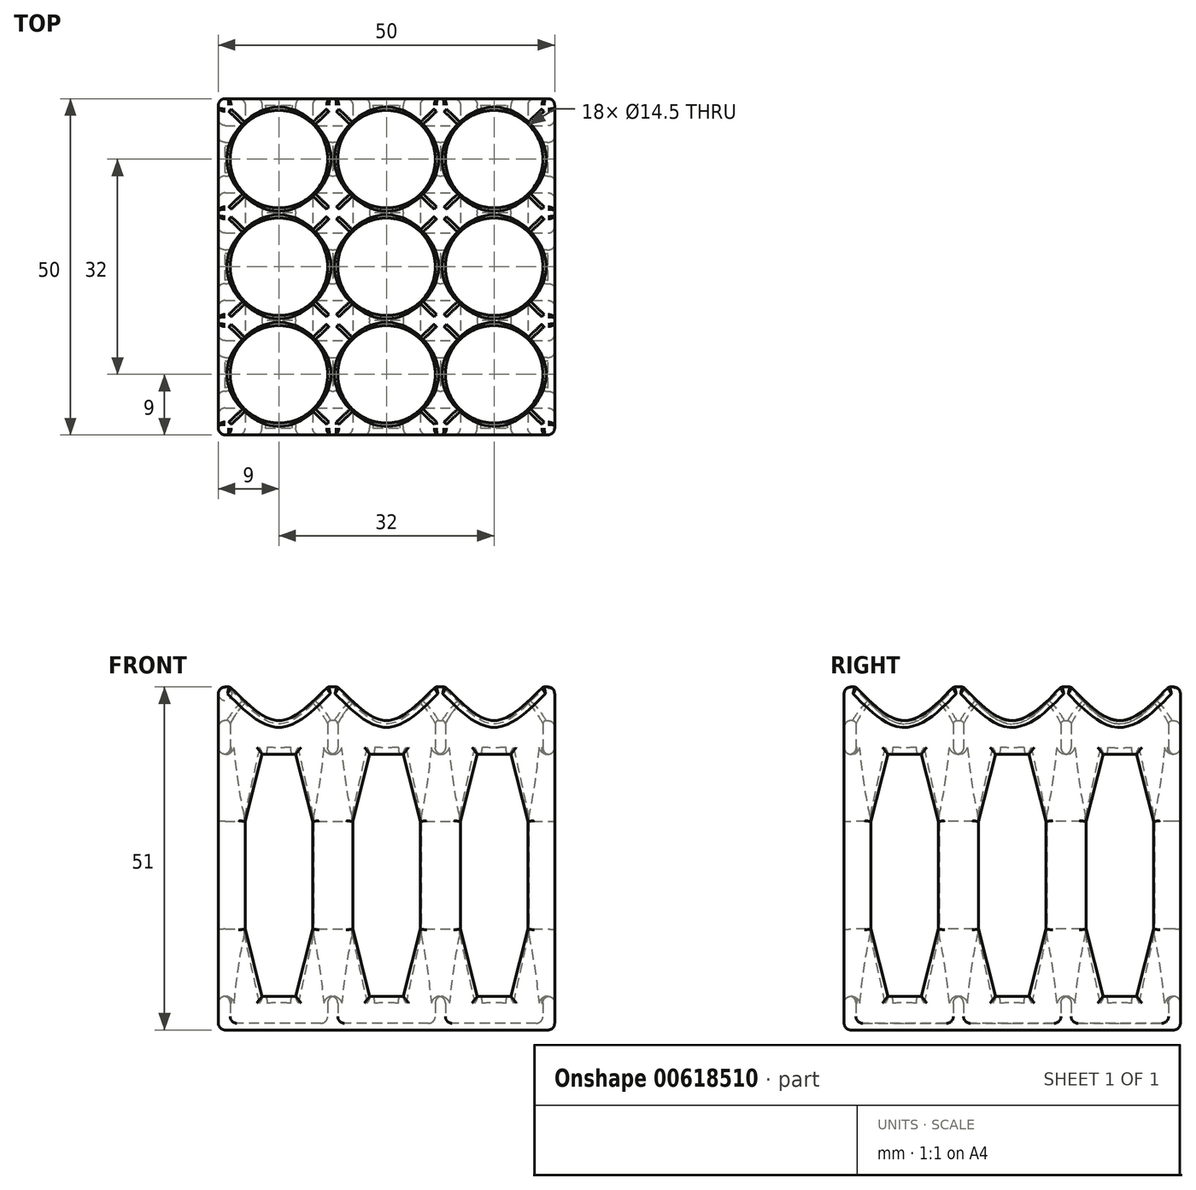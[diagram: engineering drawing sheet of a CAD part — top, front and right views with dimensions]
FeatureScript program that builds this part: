
annotation { "Feature Type Name" : "Feature", "Feature Type Description" : "" }
export const myFeature = defineFeature(function(context is Context, id is Id, definition is map)
    precondition{}
    {
        {
            var Q0;
            Q0=qCreatedBy(makeId("Top.planeOp"),FACE);
            var sketch = newSketch(context, id + "F0", { "sketchPlane" : qUnion([Q0])});
            skLineSegment(sketch, "E0.bottom", {"start": v(24, -24) * mm, "end": v(-24, -24) * mm});
            skLineSegment(sketch, "E0.top", {"start": v(24, 24) * mm, "end": v(-24, 24) * mm});
            skLineSegment(sketch, "E0.left", {"start": v(24, -24) * mm, "end": v(24, 24) * mm});
            skLineSegment(sketch, "E0.right", {"start": v(-24, -24) * mm, "end": v(-24, 24) * mm});
            skPoint(sketch, "E0.middle", {"position": v(0, 0) * mm});
            skLineSegment(sketch, "E1.0", {"start": v(25, 25) * mm, "end": v(-25, 25) * mm});
            skLineSegment(sketch, "E1.1", {"start": v(25, -25) * mm, "end": v(25, 25) * mm});
            skLineSegment(sketch, "E1.2", {"start": v(25, -25) * mm, "end": v(-25, -25) * mm});
            skLineSegment(sketch, "E1.3", {"start": v(-25, -25) * mm, "end": v(-25, 25) * mm});
            skLineSegment(sketch, "E2", {"start": v(-8, 24) * mm, "end": v(-8, -24) * mm});
            skLineSegment(sketch, "E3", {"start": v(8, 24) * mm, "end": v(8, -24) * mm});
            skLineSegment(sketch, "E4", {"start": v(-24, -8) * mm, "end": v(24, -8) * mm});
            skLineSegment(sketch, "E5", {"start": v(-24, 8) * mm, "end": v(24, 8) * mm});
            skPoint(sketch, "E6", {"position": v(-16, -16) * mm});
            skPoint(sketch, "E7", {"position": v(0, -16) * mm});
            skPoint(sketch, "E8", {"position": v(16, -16) * mm});
            skPoint(sketch, "E9", {"position": v(16, 0) * mm});
            skPoint(sketch, "E10", {"position": v(-16, 0) * mm});
            skPoint(sketch, "E11", {"position": v(-16, 16) * mm});
            skPoint(sketch, "E12", {"position": v(0, 16) * mm});
            skPoint(sketch, "E13", {"position": v(16, 16) * mm});
            skPoint(sketch, "E14", {"position": v(-8, 8) * mm});
            skPoint(sketch, "E15", {"position": v(8, 8) * mm});
            skPoint(sketch, "E16", {"position": v(-8, -8) * mm});
            skPoint(sketch, "E17", {"position": v(8, -8) * mm});
            skCircle(sketch, "E18", {"center": v(-16, -16) * mm, "radius": 7.25 * mm});
            skCircle(sketch, "E19", {"center": v(0, -16) * mm, "radius": 7.25 * mm});
            skCircle(sketch, "E20", {"center": v(16, -16) * mm, "radius": 7.25 * mm});
            skCircle(sketch, "E21", {"center": v(16, 0) * mm, "radius": 7.25 * mm});
            skCircle(sketch, "E22", {"center": v(0, 0) * mm, "radius": 7.25 * mm});
            skCircle(sketch, "E23", {"center": v(-16, 0) * mm, "radius": 7.25 * mm});
            skCircle(sketch, "E24", {"center": v(-16, 16) * mm, "radius": 7.25 * mm});
            skCircle(sketch, "E25", {"center": v(0, 16) * mm, "radius": 7.25 * mm});
            skCircle(sketch, "E26", {"center": v(16, 16) * mm, "radius": 7.25 * mm});
            skSolve(sketch);
        }
        {
            var Q0;
            Q0=qCreatedBy(makeId("Front.planeOp"),FACE);
            var sketch = newSketch(context, id + "F1", { "sketchPlane" : qUnion([Q0])});
            skPoint(sketch, "E27", {"position": v(-25, 0) * mm});
            skPoint(sketch, "E28", {"position": v(25, 0) * mm});
            skLineSegment(sketch, "E29.bottom", {"start": v(-25, 0) * mm, "end": v(25, 0) * mm});
            skLineSegment(sketch, "E29.top", {"start": v(-25, 50) * mm, "end": v(25, 50) * mm});
            skLineSegment(sketch, "E29.left", {"start": v(-25, 0) * mm, "end": v(-25, 50) * mm});
            skLineSegment(sketch, "E29.right", {"start": v(25, 0) * mm, "end": v(25, 50) * mm});
            skLineSegment(sketch, "E30.top", {"start": v(-25, -1) * mm, "end": v(25, -1) * mm});
            skLineSegment(sketch, "E30.left", {"start": v(-25, 0) * mm, "end": v(-25, -1) * mm});
            skLineSegment(sketch, "E30.right", {"start": v(25, 0) * mm, "end": v(25, -1) * mm});
            skSolve(sketch);
        }
        {
            var Q0;
            Q0=qSketchRegion(id+"F1",true);
            var Q1;
            Q1=sQuery(id+"F0.wireOp",VERTEX,"E1.3.start");
            var Q2;
            Q2=sQuery(id+"F0.wireOp",VERTEX,"E1.0.end");
            extrude(context, id + "F2", {"entities" : qUnion([Q0]), "endBound" : BoundingType.UP_TO_VERTEX, "endBoundEntityVertex" : qUnion([Q1]), "depth" : 50 * mm, "hasSecondDirection" : true, "secondDirectionBound" : SecondDirectionBoundingType.UP_TO_VERTEX, "secondDirectionOppositeDirection" : true, "secondDirectionBoundEntityVertex" : qUnion([Q2]), "secondDirectionDepth" : 25 * mm});
        }
        {
            var Q0;
            Q0=makeQuery(id+"F0.imprint","IMPRINT",FACE,{"disambiguationData":[TD([[makeQuery(id+"F0.imprint","IMPRINT",EDGE,{"derivedFrom":sQuery(id+"F0.wireOp",EDGE,"E24")}),1.0]])]});
            var Q1;
            Q1=makeQuery(id+"F0.imprint","IMPRINT",FACE,{"disambiguationData":[TD([[makeQuery(id+"F0.imprint","IMPRINT",EDGE,{"derivedFrom":sQuery(id+"F0.wireOp",EDGE,"E25")}),1.0]])]});
            var Q2;
            Q2=makeQuery(id+"F0.imprint","IMPRINT",FACE,{"disambiguationData":[TD([[makeQuery(id+"F0.imprint","IMPRINT",EDGE,{"derivedFrom":sQuery(id+"F0.wireOp",EDGE,"E26")}),1.0]])]});
            var Q3;
            Q3=makeQuery(id+"F0.imprint","IMPRINT",FACE,{"disambiguationData":[TD([[makeQuery(id+"F0.imprint","IMPRINT",EDGE,{"derivedFrom":sQuery(id+"F0.wireOp",EDGE,"E23")}),1.0]])]});
            var Q4;
            Q4=makeQuery(id+"F0.imprint","IMPRINT",FACE,{"disambiguationData":[TD([[makeQuery(id+"F0.imprint","IMPRINT",EDGE,{"derivedFrom":sQuery(id+"F0.wireOp",EDGE,"E22")}),1.0]])]});
            var Q5;
            Q5=makeQuery(id+"F0.imprint","IMPRINT",FACE,{"disambiguationData":[TD([[makeQuery(id+"F0.imprint","IMPRINT",EDGE,{"derivedFrom":sQuery(id+"F0.wireOp",EDGE,"E21")}),1.0]])]});
            var Q6;
            Q6=makeQuery(id+"F0.imprint","IMPRINT",FACE,{"disambiguationData":[TD([[makeQuery(id+"F0.imprint","IMPRINT",EDGE,{"derivedFrom":sQuery(id+"F0.wireOp",EDGE,"E20")}),1.0]])]});
            var Q7;
            Q7=makeQuery(id+"F0.imprint","IMPRINT",FACE,{"disambiguationData":[TD([[makeQuery(id+"F0.imprint","IMPRINT",EDGE,{"derivedFrom":sQuery(id+"F0.wireOp",EDGE,"E19")}),1.0]])]});
            var Q8;
            Q8=makeQuery(id+"F0.imprint","IMPRINT",FACE,{"disambiguationData":[TD([[makeQuery(id+"F0.imprint","IMPRINT",EDGE,{"derivedFrom":sQuery(id+"F0.wireOp",EDGE,"E18")}),1.0]])]});
            var Q9;
            Q9=sQuery(id+"F1.wireOp",VERTEX,"E29.left.end");
            extrude(context, id + "F3", {"entities" : qUnion([Q0, Q1, Q2, Q3, Q4, Q5, Q6, Q7, Q8]), "operationType" : NewBodyOperationType.REMOVE, "endBound" : BoundingType.UP_TO_VERTEX, "endBoundEntityVertex" : qUnion([Q9]), "depth" : 55.6 * mm});
        }
        {
            var Q0;
            Q0=makeQuery(id+"F2.opExtrude","SWEPT_FACE",FACE,{"disambiguationData":[OSD([sQuery(id+"F1.wireOp",EDGE,"E29.top")])]});
            var sketch = newSketch(context, id + "F4", { "sketchPlane" : qUnion([Q0])});
            skPoint(sketch, "E31", {"position": v(-16, -16) * mm});
            skPoint(sketch, "E32", {"position": v(0, -16) * mm});
            skPoint(sketch, "E33", {"position": v(16, -16) * mm});
            skPoint(sketch, "E34", {"position": v(-8.75, -16) * mm});
            skLineSegment(sketch, "E35", {"start": v(-16, -16) * mm, "end": v(16, -16) * mm});
            skLineSegment(sketch, "E36", {"start": v(16, -16) * mm, "end": v(23.25, -16) * mm});
            skLineSegment(sketch, "E37", {"start": v(-16, -16) * mm, "end": v(-23.25, -16) * mm});
            skPoint(sketch, "E38", {"position": v(-23.25, -16) * mm});
            skPoint(sketch, "E39", {"position": v(-7.25, -16) * mm});
            skPoint(sketch, "E40", {"position": v(7.25, -16) * mm});
            skPoint(sketch, "E41", {"position": v(8.75, -16) * mm});
            skPoint(sketch, "E42", {"position": v(23.25, -16) * mm});
            skPoint(sketch, "E43", {"position": v(16, 0) * mm});
            skPoint(sketch, "E44", {"position": v(16, 16) * mm});
            skLineSegment(sketch, "E45", {"start": v(16, -16) * mm, "end": v(16, 16) * mm});
            skLineSegment(sketch, "E46", {"start": v(16, 16) * mm, "end": v(16, 23.25) * mm});
            skLineSegment(sketch, "E47", {"start": v(16, -16) * mm, "end": v(16, -23.25) * mm});
            skPoint(sketch, "E48", {"position": v(16, -23.25) * mm});
            skPoint(sketch, "E49", {"position": v(16, -8.75) * mm});
            skPoint(sketch, "E50", {"position": v(16, -7.25) * mm});
            skPoint(sketch, "E51", {"position": v(16, 7.25) * mm});
            skPoint(sketch, "E52", {"position": v(16, 8.75) * mm});
            skPoint(sketch, "E53", {"position": v(16, 23.25) * mm});
            skSolve(sketch);
        }
        {
            var Q0;
            Q0=makeQuery(id+"F2.opExtrude","CAP_FACE",FACE,{"disambiguationData":[OSD([sQuery(id+"F1.wireOp",EDGE,"E29.top"),sQuery(id+"F1.wireOp",EDGE,"E29.left"),sQuery(id+"F1.wireOp",EDGE,"E29.right"),sQuery(id+"F1.wireOp",EDGE,"E30.top"),sQuery(id+"F1.wireOp",EDGE,"E30.left"),sQuery(id+"F1.wireOp",EDGE,"E30.right")])],"isStart":false});
            var sketch = newSketch(context, id + "F5", { "sketchPlane" : qUnion([Q0])});
            skPoint(sketch, "E54", {"position": v(-23.25, 50) * mm});
            skPoint(sketch, "E55", {"position": v(-8.75, 50) * mm});
            skPoint(sketch, "E56", {"position": v(-16, 45) * mm});
            skPoint(sketch, "E57", {"position": v(-7.25, 50) * mm});
            skPoint(sketch, "E58", {"position": v(7.25, 50) * mm});
            skPoint(sketch, "E59", {"position": v(8.75, 50) * mm});
            skPoint(sketch, "E60", {"position": v(23.25, 50) * mm});
            skFitSpline(sketch, "E61", {"points": [v(-23.25, 50) * mm, v(-16, 45) * mm, v(-8.75, 50) * mm], "startDerivative": vector(15.5, -15) * mm, "endDerivative": vector(15.5, 15) * mm});
            skFitSpline(sketch, "E62", {"points": [v(-7.25, 50) * mm, v(0, 45) * mm, v(7.25, 50) * mm], "startDerivative": vector(15.5, -15) * mm, "endDerivative": vector(15.5, 15) * mm});
            skFitSpline(sketch, "E63", {"points": [v(8.75, 50) * mm, v(16, 45) * mm, v(23.25, 50) * mm], "startDerivative": vector(15.5, -15) * mm, "endDerivative": vector(15.5, 15) * mm});
            skSolve(sketch);
        }
        {
            var Q0;
            {var subQ0=sQuery(id+"F5.wireOp",EDGE,"E61");Q0=makeQuery(id+"F5.imprint","IMPRINT",FACE,{"disambiguationData":[TD([[makeQuery(id+"F5.imprint","IMPRINT",EDGE,{"derivedFrom":subQ0}),1.0]])]});}
            var Q1;
            {var subQ0=sQuery(id+"F5.wireOp",EDGE,"E62");Q1=makeQuery(id+"F5.imprint","IMPRINT",FACE,{"disambiguationData":[TD([[makeQuery(id+"F5.imprint","IMPRINT",EDGE,{"derivedFrom":subQ0}),1.0]])]});}
            var Q2;
            {var subQ0=sQuery(id+"F5.wireOp",EDGE,"E63");Q2=makeQuery(id+"F5.imprint","IMPRINT",FACE,{"disambiguationData":[TD([[makeQuery(id+"F5.imprint","IMPRINT",EDGE,{"derivedFrom":subQ0}),1.0]])]});}
            var Q3;
            Q3=makeQuery(id+"F2.opExtrude","CAP_VERTEX",VERTEX,{"disambiguationData":[OSD([sQuery(id+"F1.wireOp",EDGE,"E29.top"),sQuery(id+"F1.wireOp",EDGE,"E29.left"),sQuery(id+"F1.wireOp",EDGE,"E30.left")])],"isStart":true});
            extrude(context, id + "F6", {"entities" : qUnion([Q0, Q1, Q2]), "operationType" : NewBodyOperationType.REMOVE, "endBound" : BoundingType.UP_TO_VERTEX, "oppositeDirection" : true, "endBoundEntityVertex" : qUnion([Q3]), "depth" : 25 * mm});
        }
        {
            var Q0;
            Q0=makeQuery(id+"F2.opExtrude","SWEPT_FACE",FACE,{"disambiguationData":[OSD([sQuery(id+"F1.wireOp",EDGE,"E29.right"),sQuery(id+"F1.wireOp",EDGE,"E30.right")])]});
            var sketch = newSketch(context, id + "F7", { "sketchPlane" : qUnion([Q0])});
            skPoint(sketch, "E64", {"position": v(-23.25, 50) * mm});
            skPoint(sketch, "E65", {"position": v(-16, 45) * mm});
            skPoint(sketch, "E66", {"position": v(-8.75, 50) * mm});
            skPoint(sketch, "E67", {"position": v(-7.25, 50) * mm});
            skPoint(sketch, "E68", {"position": v(0, 45) * mm});
            skPoint(sketch, "E69", {"position": v(7.25, 50) * mm});
            skPoint(sketch, "E70", {"position": v(8.75, 50) * mm});
            skPoint(sketch, "E71", {"position": v(16, 45) * mm});
            skPoint(sketch, "E72", {"position": v(23.25, 50) * mm});
            skFitSpline(sketch, "E73", {"points": [v(-23.25, 50) * mm, v(-16, 45) * mm, v(-8.75, 50) * mm], "startDerivative": vector(14.5, -15) * mm, "endDerivative": vector(14.5, 15) * mm});
            skFitSpline(sketch, "E74", {"points": [v(-7.25, 50) * mm, v(0, 45) * mm, v(7.25, 50) * mm], "startDerivative": vector(14.5, -15) * mm, "endDerivative": vector(14.5, 15) * mm});
            skFitSpline(sketch, "E75", {"points": [v(8.75, 50) * mm, v(16, 45) * mm, v(23.25, 50) * mm], "startDerivative": vector(14.5, -15) * mm, "endDerivative": vector(14.5, 15) * mm});
            skSolve(sketch);
        }
        {
            var Q0;
            {var subQ0=sQuery(id+"F7.wireOp",EDGE,"E73");Q0=makeQuery(id+"F7.imprint","IMPRINT",FACE,{"disambiguationData":[TD([[makeQuery(id+"F7.imprint","IMPRINT",EDGE,{"derivedFrom":subQ0}),1.0]])]});}
            var Q1;
            {var subQ0=sQuery(id+"F7.wireOp",EDGE,"E74");Q1=makeQuery(id+"F7.imprint","IMPRINT",FACE,{"disambiguationData":[TD([[makeQuery(id+"F7.imprint","IMPRINT",EDGE,{"derivedFrom":subQ0}),1.0]])]});}
            var Q2;
            {var subQ0=sQuery(id+"F7.wireOp",EDGE,"E75");Q2=makeQuery(id+"F7.imprint","IMPRINT",FACE,{"disambiguationData":[TD([[makeQuery(id+"F7.imprint","IMPRINT",EDGE,{"derivedFrom":subQ0}),1.0]])]});}
            var Q3;
            Q3=makeQuery(id+"F2.opExtrude","CAP_VERTEX",VERTEX,{"disambiguationData":[OSD([sQuery(id+"F1.wireOp",EDGE,"E29.top"),sQuery(id+"F1.wireOp",EDGE,"E29.left"),sQuery(id+"F1.wireOp",EDGE,"E30.left")])],"isStart":false});
            extrude(context, id + "F8", {"entities" : qUnion([Q0, Q1, Q2]), "operationType" : NewBodyOperationType.REMOVE, "endBound" : BoundingType.UP_TO_VERTEX, "oppositeDirection" : true, "endBoundEntityVertex" : qUnion([Q3]), "depth" : 25 * mm});
        }
        {
            var Q0;
            {var subQ4=sQuery(id+"F5.wireOp",EDGE,"E61");Q0=makeQuery(id+"F5.imprint","IMPRINT",FACE,{"disambiguationData":[TD([[makeQuery(id+"F5.imprint","IMPRINT",EDGE,{"derivedFrom":subQ4}),-1.0]])]});}
            var sketch = newSketch(context, id + "F9", { "sketchPlane" : qUnion([Q0])});
            skPoint(sketch, "E76", {"position": v(0, 50) * mm});
            skLineSegment(sketch, "E77", {"start": v(0, 50) * mm, "end": v(0, -1) * mm});
            skPoint(sketch, "E78", {"position": v(16, 50) * mm});
            skLineSegment(sketch, "E79", {"start": v(16, 50) * mm, "end": v(16, -1) * mm});
            skPoint(sketch, "E80", {"position": v(-5, 30) * mm});
            skPoint(sketch, "E81", {"position": v(-5, 14) * mm});
            skPoint(sketch, "E82", {"position": v(5, 14) * mm});
            skPoint(sketch, "E83", {"position": v(5, 30) * mm});
            skPoint(sketch, "E84", {"position": v(-2.5, 40) * mm});
            skPoint(sketch, "E85", {"position": v(-2.5, 4) * mm});
            skPoint(sketch, "E86", {"position": v(2.5, 40) * mm});
            skPoint(sketch, "E87", {"position": v(2.5, 4) * mm});
            skPoint(sketch, "E88", {"position": v(-16, 50) * mm});
            skLineSegment(sketch, "E89", {"start": v(-16, 50) * mm, "end": v(-16, -1) * mm});
            skPoint(sketch, "E90", {"position": v(-21, 30) * mm});
            skPoint(sketch, "E91", {"position": v(-21, 14) * mm});
            skPoint(sketch, "E92", {"position": v(-11, 14) * mm});
            skPoint(sketch, "E93", {"position": v(-11, 30) * mm});
            skPoint(sketch, "E94", {"position": v(-18.5, 40) * mm});
            skPoint(sketch, "E95", {"position": v(-18.5, 4) * mm});
            skPoint(sketch, "E96", {"position": v(-13.5, 40) * mm});
            skPoint(sketch, "E97", {"position": v(-13.5, 4) * mm});
            skPoint(sketch, "E98", {"position": v(11, 30) * mm});
            skPoint(sketch, "E99", {"position": v(11, 14) * mm});
            skPoint(sketch, "E100", {"position": v(21, 14) * mm});
            skPoint(sketch, "E101", {"position": v(21, 30) * mm});
            skPoint(sketch, "E102", {"position": v(13.5, 40) * mm});
            skPoint(sketch, "E103", {"position": v(13.5, 4) * mm});
            skPoint(sketch, "E104", {"position": v(18.5, 40) * mm});
            skPoint(sketch, "E105", {"position": v(18.5, 4) * mm});
            skLineSegment(sketch, "E106", {"start": v(-18.5, 40) * mm, "end": v(-21, 30) * mm});
            skLineSegment(sketch, "E107", {"start": v(-21, 14) * mm, "end": v(-18.5, 4) * mm});
            skLineSegment(sketch, "E108", {"start": v(-13.5, 4) * mm, "end": v(-11, 14) * mm});
            skLineSegment(sketch, "E109", {"start": v(-11, 30) * mm, "end": v(-13.5, 40) * mm});
            skLineSegment(sketch, "E110", {"start": v(-18.5, 40) * mm, "end": v(-13.5, 40) * mm});
            skLineSegment(sketch, "E111", {"start": v(-11, 30) * mm, "end": v(-11, 14) * mm});
            skLineSegment(sketch, "E112", {"start": v(-21, 14) * mm, "end": v(-21, 30) * mm});
            skLineSegment(sketch, "E113", {"start": v(-18.5, 4) * mm, "end": v(-13.5, 4) * mm});
            skLineSegment(sketch, "E114", {"start": v(-2.5, 40) * mm, "end": v(-5, 30) * mm});
            skLineSegment(sketch, "E115", {"start": v(-5, 30) * mm, "end": v(-5, 14) * mm});
            skLineSegment(sketch, "E116", {"start": v(-5, 14) * mm, "end": v(-2.5, 4) * mm});
            skLineSegment(sketch, "E117", {"start": v(-2.5, 4) * mm, "end": v(2.5, 4) * mm});
            skLineSegment(sketch, "E118", {"start": v(2.5, 4) * mm, "end": v(5, 14) * mm});
            skLineSegment(sketch, "E119", {"start": v(5, 14) * mm, "end": v(5, 30) * mm});
            skLineSegment(sketch, "E120", {"start": v(2.5, 40) * mm, "end": v(5, 30) * mm});
            skLineSegment(sketch, "E121", {"start": v(2.5, 40) * mm, "end": v(-2.5, 40) * mm});
            skLineSegment(sketch, "E122", {"start": v(13.5, 40) * mm, "end": v(18.5, 40) * mm});
            skLineSegment(sketch, "E123", {"start": v(18.5, 40) * mm, "end": v(21, 30) * mm});
            skLineSegment(sketch, "E124", {"start": v(21, 30) * mm, "end": v(21, 14) * mm});
            skLineSegment(sketch, "E125", {"start": v(21, 14) * mm, "end": v(18.5, 4) * mm});
            skLineSegment(sketch, "E126", {"start": v(13.5, 4) * mm, "end": v(18.5, 4) * mm});
            skLineSegment(sketch, "E127", {"start": v(13.5, 4) * mm, "end": v(11, 14) * mm});
            skLineSegment(sketch, "E128", {"start": v(11, 14) * mm, "end": v(11, 30) * mm});
            skLineSegment(sketch, "E129", {"start": v(11, 30) * mm, "end": v(13.5, 40) * mm});
            skSolve(sketch);
        }
        {
            var Q0;
            {var subQ4=sQuery(id+"F9.wireOp",EDGE,"E108");Q0=makeQuery(id+"F9.imprint","IMPRINT",FACE,{"disambiguationData":[TD([[makeQuery(id+"F9.imprint","IMPRINT",EDGE,{"derivedFrom":subQ4}),1.0]])]});}
            var Q1;
            {var subQ1=sQuery(id+"F9.wireOp",EDGE,"E106");Q1=makeQuery(id+"F9.imprint","IMPRINT",FACE,{"disambiguationData":[TD([[makeQuery(id+"F9.imprint","IMPRINT",EDGE,{"derivedFrom":subQ1}),1.0]])]});}
            var Q2;
            {var subQ0=sQuery(id+"F9.wireOp",EDGE,"E114");Q2=makeQuery(id+"F9.imprint","IMPRINT",FACE,{"disambiguationData":[TD([[makeQuery(id+"F9.imprint","IMPRINT",EDGE,{"derivedFrom":subQ0}),1.0]])]});}
            var Q3;
            {var subQ0=sQuery(id+"F9.wireOp",EDGE,"E118");Q3=makeQuery(id+"F9.imprint","IMPRINT",FACE,{"disambiguationData":[TD([[makeQuery(id+"F9.imprint","IMPRINT",EDGE,{"derivedFrom":subQ0}),1.0]])]});}
            var Q4;
            {var subQ0=sQuery(id+"F9.wireOp",EDGE,"E127");Q4=makeQuery(id+"F9.imprint","IMPRINT",FACE,{"disambiguationData":[TD([[makeQuery(id+"F9.imprint","IMPRINT",EDGE,{"derivedFrom":subQ0}),-1.0]])]});}
            var Q5;
            {var subQ0=sQuery(id+"F9.wireOp",EDGE,"E123");Q5=makeQuery(id+"F9.imprint","IMPRINT",FACE,{"disambiguationData":[TD([[makeQuery(id+"F9.imprint","IMPRINT",EDGE,{"derivedFrom":subQ0}),-1.0]])]});}
            var Q6;
            Q6=makeQuery(id+"F2.opExtrude","CAP_VERTEX",VERTEX,{"disambiguationData":[OSD([sQuery(id+"F1.wireOp",EDGE,"E29.left"),sQuery(id+"F1.wireOp",EDGE,"E30.top"),sQuery(id+"F1.wireOp",EDGE,"E30.left")])],"isStart":true});
            extrude(context, id + "F10", {"entities" : qUnion([Q0, Q1, Q2, Q3, Q4, Q5]), "operationType" : NewBodyOperationType.REMOVE, "endBound" : BoundingType.UP_TO_VERTEX, "oppositeDirection" : true, "endBoundEntityVertex" : qUnion([Q6]), "depth" : 25 * mm});
        }
        {
            var Q0;
            Q0=makeQuery(id+"F2.opExtrude","SWEPT_FACE",FACE,{"disambiguationData":[OSD([sQuery(id+"F1.wireOp",EDGE,"E29.right"),sQuery(id+"F1.wireOp",EDGE,"E30.right")])]});
            var sketch = newSketch(context, id + "F11", { "sketchPlane" : qUnion([Q0])});
            skPoint(sketch, "E130", {"position": v(0, 50) * mm});
            skLineSegment(sketch, "E131", {"start": v(0, 50) * mm, "end": v(0, -1) * mm});
            skPoint(sketch, "E132", {"position": v(16, 50) * mm});
            skLineSegment(sketch, "E133", {"start": v(16, 50) * mm, "end": v(16, -1) * mm});
            skPoint(sketch, "E134", {"position": v(-5, 30) * mm});
            skPoint(sketch, "E135", {"position": v(-5, 14) * mm});
            skPoint(sketch, "E136", {"position": v(5, 14) * mm});
            skPoint(sketch, "E137", {"position": v(5, 30) * mm});
            skPoint(sketch, "E138", {"position": v(-2.5, 40) * mm});
            skPoint(sketch, "E139", {"position": v(-2.5, 4) * mm});
            skPoint(sketch, "E140", {"position": v(2.5, 40) * mm});
            skPoint(sketch, "E141", {"position": v(2.5, 4) * mm});
            skPoint(sketch, "E142", {"position": v(-16, 50) * mm});
            skLineSegment(sketch, "E143", {"start": v(-16, 50) * mm, "end": v(-16, -1) * mm});
            skPoint(sketch, "E144", {"position": v(-21, 30) * mm});
            skPoint(sketch, "E145", {"position": v(-21, 14) * mm});
            skPoint(sketch, "E146", {"position": v(-11, 14) * mm});
            skPoint(sketch, "E147", {"position": v(-11, 30) * mm});
            skPoint(sketch, "E148", {"position": v(-18.5, 40) * mm});
            skPoint(sketch, "E149", {"position": v(-18.5, 4) * mm});
            skPoint(sketch, "E150", {"position": v(-13.5, 40) * mm});
            skPoint(sketch, "E151", {"position": v(-13.5, 4) * mm});
            skPoint(sketch, "E152", {"position": v(11, 30) * mm});
            skPoint(sketch, "E153", {"position": v(11, 14) * mm});
            skPoint(sketch, "E154", {"position": v(21, 14) * mm});
            skPoint(sketch, "E155", {"position": v(21, 30) * mm});
            skPoint(sketch, "E156", {"position": v(13.5, 40) * mm});
            skPoint(sketch, "E157", {"position": v(13.5, 4) * mm});
            skPoint(sketch, "E158", {"position": v(18.5, 40) * mm});
            skPoint(sketch, "E159", {"position": v(18.5, 4) * mm});
            skLineSegment(sketch, "E160", {"start": v(-18.5, 40) * mm, "end": v(-21, 30) * mm});
            skLineSegment(sketch, "E161", {"start": v(-21, 14) * mm, "end": v(-18.5, 4) * mm});
            skLineSegment(sketch, "E162", {"start": v(-13.5, 4) * mm, "end": v(-11, 14) * mm});
            skLineSegment(sketch, "E163", {"start": v(-11, 30) * mm, "end": v(-13.5, 40) * mm});
            skLineSegment(sketch, "E164", {"start": v(-18.5, 40) * mm, "end": v(-13.5, 40) * mm});
            skLineSegment(sketch, "E165", {"start": v(-11, 30) * mm, "end": v(-11, 14) * mm});
            skLineSegment(sketch, "E166", {"start": v(-21, 14) * mm, "end": v(-21, 30) * mm});
            skLineSegment(sketch, "E167", {"start": v(-18.5, 4) * mm, "end": v(-13.5, 4) * mm});
            skLineSegment(sketch, "E168", {"start": v(-2.5, 40) * mm, "end": v(-5, 30) * mm});
            skLineSegment(sketch, "E169", {"start": v(-5, 30) * mm, "end": v(-5, 14) * mm});
            skLineSegment(sketch, "E170", {"start": v(-5, 14) * mm, "end": v(-2.5, 4) * mm});
            skLineSegment(sketch, "E171", {"start": v(-2.5, 4) * mm, "end": v(2.5, 4) * mm});
            skLineSegment(sketch, "E172", {"start": v(2.5, 4) * mm, "end": v(5, 14) * mm});
            skLineSegment(sketch, "E173", {"start": v(5, 14) * mm, "end": v(5, 30) * mm});
            skLineSegment(sketch, "E174", {"start": v(2.5, 40) * mm, "end": v(5, 30) * mm});
            skLineSegment(sketch, "E175", {"start": v(2.5, 40) * mm, "end": v(-2.5, 40) * mm});
            skLineSegment(sketch, "E176", {"start": v(13.5, 40) * mm, "end": v(18.5, 40) * mm});
            skLineSegment(sketch, "E177", {"start": v(18.5, 40) * mm, "end": v(21, 30) * mm});
            skLineSegment(sketch, "E178", {"start": v(21, 30) * mm, "end": v(21, 14) * mm});
            skLineSegment(sketch, "E179", {"start": v(21, 14) * mm, "end": v(18.5, 4) * mm});
            skLineSegment(sketch, "E180", {"start": v(13.5, 4) * mm, "end": v(18.5, 4) * mm});
            skLineSegment(sketch, "E181", {"start": v(13.5, 4) * mm, "end": v(11, 14) * mm});
            skLineSegment(sketch, "E182", {"start": v(11, 14) * mm, "end": v(11, 30) * mm});
            skLineSegment(sketch, "E183", {"start": v(11, 30) * mm, "end": v(13.5, 40) * mm});
            skSolve(sketch);
        }
        {
            var Q0;
            {var subQ1=sQuery(id+"F11.wireOp",EDGE,"E160");Q0=makeQuery(id+"F11.imprint","IMPRINT",FACE,{"disambiguationData":[TD([[makeQuery(id+"F11.imprint","IMPRINT",EDGE,{"derivedFrom":subQ1}),1.0]])]});}
            var Q1;
            {var subQ4=sQuery(id+"F11.wireOp",EDGE,"E162");Q1=makeQuery(id+"F11.imprint","IMPRINT",FACE,{"disambiguationData":[TD([[makeQuery(id+"F11.imprint","IMPRINT",EDGE,{"derivedFrom":subQ4}),1.0]])]});}
            var Q2;
            {var subQ0=sQuery(id+"F11.wireOp",EDGE,"E168");Q2=makeQuery(id+"F11.imprint","IMPRINT",FACE,{"disambiguationData":[TD([[makeQuery(id+"F11.imprint","IMPRINT",EDGE,{"derivedFrom":subQ0}),1.0]])]});}
            var Q3;
            {var subQ0=sQuery(id+"F11.wireOp",EDGE,"E172");Q3=makeQuery(id+"F11.imprint","IMPRINT",FACE,{"disambiguationData":[TD([[makeQuery(id+"F11.imprint","IMPRINT",EDGE,{"derivedFrom":subQ0}),1.0]])]});}
            var Q4;
            {var subQ0=sQuery(id+"F11.wireOp",EDGE,"E181");Q4=makeQuery(id+"F11.imprint","IMPRINT",FACE,{"disambiguationData":[TD([[makeQuery(id+"F11.imprint","IMPRINT",EDGE,{"derivedFrom":subQ0}),-1.0]])]});}
            var Q5;
            {var subQ0=sQuery(id+"F11.wireOp",EDGE,"E177");Q5=makeQuery(id+"F11.imprint","IMPRINT",FACE,{"disambiguationData":[TD([[makeQuery(id+"F11.imprint","IMPRINT",EDGE,{"derivedFrom":subQ0}),-1.0]])]});}
            var Q6;
            Q6=makeQuery(id+"F2.opExtrude","CAP_VERTEX",VERTEX,{"disambiguationData":[OSD([sQuery(id+"F1.wireOp",EDGE,"E29.left"),sQuery(id+"F1.wireOp",EDGE,"E30.top"),sQuery(id+"F1.wireOp",EDGE,"E30.left")])],"isStart":false});
            extrude(context, id + "F12", {"entities" : qUnion([Q0, Q1, Q2, Q3, Q4, Q5]), "operationType" : NewBodyOperationType.REMOVE, "endBound" : BoundingType.UP_TO_VERTEX, "oppositeDirection" : true, "endBoundEntityVertex" : qUnion([Q6]), "depth" : 25 * mm});
        }
        {
            var Q0;
            Q0=makeQuery(id+"F2.opExtrude","SWEPT_FACE",FACE,{"disambiguationData":[OSD([sQuery(id+"F1.wireOp",EDGE,"E30.top")])]});
            var Q1;
            Q1=makeQuery(id+"F2.opExtrude","SWEPT_FACE",FACE,{"disambiguationData":[OSD([sQuery(id+"F1.wireOp",EDGE,"E29.right"),sQuery(id+"F1.wireOp",EDGE,"E30.right")])]});
            var Q2;
            Q2=makeQuery(id+"F2.opExtrude","CAP_FACE",FACE,{"disambiguationData":[OSD([sQuery(id+"F1.wireOp",EDGE,"E29.top"),sQuery(id+"F1.wireOp",EDGE,"E29.left"),sQuery(id+"F1.wireOp",EDGE,"E29.right"),sQuery(id+"F1.wireOp",EDGE,"E30.top"),sQuery(id+"F1.wireOp",EDGE,"E30.left"),sQuery(id+"F1.wireOp",EDGE,"E30.right")])],"isStart":false});
            var Q3;
            Q3=makeQuery(id+"F2.opExtrude","SWEPT_FACE",FACE,{"disambiguationData":[OSD([sQuery(id+"F1.wireOp",EDGE,"E29.left"),sQuery(id+"F1.wireOp",EDGE,"E30.left")])]});
            var Q4;
            Q4=makeQuery(id+"F2.opExtrude","CAP_FACE",FACE,{"disambiguationData":[OSD([sQuery(id+"F1.wireOp",EDGE,"E29.top"),sQuery(id+"F1.wireOp",EDGE,"E29.left"),sQuery(id+"F1.wireOp",EDGE,"E29.right"),sQuery(id+"F1.wireOp",EDGE,"E30.top"),sQuery(id+"F1.wireOp",EDGE,"E30.left"),sQuery(id+"F1.wireOp",EDGE,"E30.right")])],"isStart":true});
            fillet(context, id + "F13", {"entities" : qUnion([Q0, Q1, Q2, Q3, Q4]), "radius" : 1 * mm, "tangentPropagation" : true, "allowEdgeOverflow" : false});
        }
        {
            var Q0;
            Q0=makeQuery(id+"F3.boolean.opBoolean","COPY",FACE,{"derivedFrom":makeQuery(id+"F3.opExtrude","CAP_FACE",FACE,{"disambiguationData":[OSD([sQuery(id+"F0.wireOp",EDGE,"E20")])],"isStart":true})});
            var Q1;
            Q1=makeQuery(id+"F3.boolean.opBoolean","COPY",FACE,{"derivedFrom":makeQuery(id+"F3.opExtrude","CAP_FACE",FACE,{"disambiguationData":[OSD([sQuery(id+"F0.wireOp",EDGE,"E19")])],"isStart":true})});
            var Q2;
            Q2=makeQuery(id+"F3.boolean.opBoolean","COPY",FACE,{"derivedFrom":makeQuery(id+"F3.opExtrude","CAP_FACE",FACE,{"disambiguationData":[OSD([sQuery(id+"F0.wireOp",EDGE,"E18")])],"isStart":true})});
            var Q3;
            Q3=makeQuery(id+"F3.boolean.opBoolean","COPY",FACE,{"derivedFrom":makeQuery(id+"F3.opExtrude","CAP_FACE",FACE,{"disambiguationData":[OSD([sQuery(id+"F0.wireOp",EDGE,"E23")])],"isStart":true})});
            var Q4;
            Q4=makeQuery(id+"F3.boolean.opBoolean","COPY",FACE,{"derivedFrom":makeQuery(id+"F3.opExtrude","CAP_FACE",FACE,{"disambiguationData":[OSD([sQuery(id+"F0.wireOp",EDGE,"E22")])],"isStart":true})});
            var Q5;
            Q5=makeQuery(id+"F3.boolean.opBoolean","COPY",FACE,{"derivedFrom":makeQuery(id+"F3.opExtrude","CAP_FACE",FACE,{"disambiguationData":[OSD([sQuery(id+"F0.wireOp",EDGE,"E21")])],"isStart":true})});
            var Q6;
            Q6=makeQuery(id+"F3.boolean.opBoolean","COPY",FACE,{"derivedFrom":makeQuery(id+"F3.opExtrude","CAP_FACE",FACE,{"disambiguationData":[OSD([sQuery(id+"F0.wireOp",EDGE,"E26")])],"isStart":true})});
            var Q7;
            Q7=makeQuery(id+"F3.boolean.opBoolean","COPY",FACE,{"derivedFrom":makeQuery(id+"F3.opExtrude","CAP_FACE",FACE,{"disambiguationData":[OSD([sQuery(id+"F0.wireOp",EDGE,"E25")])],"isStart":true})});
            var Q8;
            Q8=makeQuery(id+"F3.boolean.opBoolean","COPY",FACE,{"derivedFrom":makeQuery(id+"F3.opExtrude","CAP_FACE",FACE,{"disambiguationData":[OSD([sQuery(id+"F0.wireOp",EDGE,"E24")])],"isStart":true})});
            fillet(context, id + "F14", {"entities" : qUnion([Q0, Q1, Q2, Q3, Q4, Q5, Q6, Q7, Q8]), "radius" : 1 * mm, "tangentPropagation" : true, "allowEdgeOverflow" : false});
        }
        {
            var Q0;
            {var subQ0=sQuery(id+"F1.wireOp",EDGE,"E29.top");var subQ1=makeQuery(id+"F2.opExtrude","SWEPT_FACE",FACE,{"disambiguationData":[OSD([subQ0])]});var subQ2=makeQuery(id+"F2.opExtrude","CAP_FACE",FACE,{"disambiguationData":[OSD([subQ0,sQuery(id+"F1.wireOp",EDGE,"E29.left"),sQuery(id+"F1.wireOp",EDGE,"E29.right"),sQuery(id+"F1.wireOp",EDGE,"E30.top"),sQuery(id+"F1.wireOp",EDGE,"E30.left"),sQuery(id+"F1.wireOp",EDGE,"E30.right")])],"isStart":false});var subQ3=makeQuery(id+"F3.boolean.opBoolean","COPY",FACE,{"derivedFrom":makeQuery(id+"F3.opExtrude","SWEPT_FACE",FACE,{"disambiguationData":[OSD([sQuery(id+"F0.wireOp",EDGE,"E19")])]})});var subQ4=makeQuery(id+"F6.opExtrude","SWEPT_FACE",FACE,{"disambiguationData":[OSD([sQuery(id+"F5.wireOp",EDGE,"E62")])]});var subQ5=makeQuery(id+"F3.boolean.opBoolean","COPY",FACE,{"derivedFrom":makeQuery(id+"F3.opExtrude","SWEPT_FACE",FACE,{"disambiguationData":[OSD([sQuery(id+"F0.wireOp",EDGE,"E20")])]})});var subQ6=makeQuery(id+"F6.opExtrude","SWEPT_FACE",FACE,{"disambiguationData":[OSD([sQuery(id+"F5.wireOp",EDGE,"E63")])]});Q0=makeQuery(id+"F8.boolean.opBoolean","COPY",FACE,{"disambiguationData":[TD([subQ1,subQ3,subQ5,makeQuery(id+"F6.boolean.opBoolean","COPY",FACE,{"disambiguationData":[TD([subQ1,subQ2,subQ3,subQ4])],"derivedFrom":subQ4}),makeQuery(id+"F6.boolean.opBoolean","COPY",FACE,{"disambiguationData":[TD([subQ1,subQ3,makeQuery(id+"F3.boolean.opBoolean","COPY",FACE,{"derivedFrom":makeQuery(id+"F3.opExtrude","SWEPT_FACE",FACE,{"disambiguationData":[OSD([sQuery(id+"F0.wireOp",EDGE,"E22")])]})}),subQ4])],"derivedFrom":subQ4}),makeQuery(id+"F6.boolean.opBoolean","COPY",FACE,{"disambiguationData":[TD([subQ1,subQ2,subQ5,subQ6])],"derivedFrom":subQ6}),makeQuery(id+"F6.boolean.opBoolean","COPY",FACE,{"disambiguationData":[TD([subQ1,subQ5,makeQuery(id+"F3.boolean.opBoolean","COPY",FACE,{"derivedFrom":makeQuery(id+"F3.opExtrude","SWEPT_FACE",FACE,{"disambiguationData":[OSD([sQuery(id+"F0.wireOp",EDGE,"E21")])]})}),subQ6])],"derivedFrom":subQ6})])],"derivedFrom":makeQuery(id+"F8.opExtrude","SWEPT_FACE",FACE,{"disambiguationData":[OSD([sQuery(id+"F7.wireOp",EDGE,"E73")])]})});}
            var Q1;
            {var subQ0=sQuery(id+"F1.wireOp",EDGE,"E29.top");var subQ1=makeQuery(id+"F6.opExtrude","SWEPT_FACE",FACE,{"disambiguationData":[OSD([sQuery(id+"F5.wireOp",EDGE,"E63")])]});Q1=makeQuery(id+"F6.boolean.opBoolean","COPY",FACE,{"disambiguationData":[TD([makeQuery(id+"F2.opExtrude","SWEPT_FACE",FACE,{"disambiguationData":[OSD([subQ0])]}),makeQuery(id+"F2.opExtrude","CAP_FACE",FACE,{"disambiguationData":[OSD([subQ0,sQuery(id+"F1.wireOp",EDGE,"E29.left"),sQuery(id+"F1.wireOp",EDGE,"E29.right"),sQuery(id+"F1.wireOp",EDGE,"E30.top"),sQuery(id+"F1.wireOp",EDGE,"E30.left"),sQuery(id+"F1.wireOp",EDGE,"E30.right")])],"isStart":false}),makeQuery(id+"F3.boolean.opBoolean","COPY",FACE,{"derivedFrom":makeQuery(id+"F3.opExtrude","SWEPT_FACE",FACE,{"disambiguationData":[OSD([sQuery(id+"F0.wireOp",EDGE,"E20")])]})}),subQ1])],"derivedFrom":subQ1});}
            var Q2;
            {var subQ0=makeQuery(id+"F3.boolean.opBoolean","COPY",FACE,{"derivedFrom":makeQuery(id+"F3.opExtrude","SWEPT_FACE",FACE,{"disambiguationData":[OSD([sQuery(id+"F0.wireOp",EDGE,"E20")])]})});var subQ1=sQuery(id+"F1.wireOp",EDGE,"E29.top");var subQ2=makeQuery(id+"F2.opExtrude","SWEPT_FACE",FACE,{"disambiguationData":[OSD([subQ1])]});var subQ3=makeQuery(id+"F6.opExtrude","SWEPT_FACE",FACE,{"disambiguationData":[OSD([sQuery(id+"F5.wireOp",EDGE,"E63")])]});var subQ4=sQuery(id+"F1.wireOp",EDGE,"E30.right");var subQ5=sQuery(id+"F1.wireOp",EDGE,"E29.right");Q2=makeQuery(id+"F8.boolean.opBoolean","COPY",FACE,{"disambiguationData":[TD([subQ2,makeQuery(id+"F2.opExtrude","SWEPT_FACE",FACE,{"disambiguationData":[OSD([subQ5,subQ4])]}),subQ0,makeQuery(id+"F6.boolean.opBoolean","COPY",FACE,{"disambiguationData":[TD([subQ2,makeQuery(id+"F2.opExtrude","CAP_FACE",FACE,{"disambiguationData":[OSD([subQ1,sQuery(id+"F1.wireOp",EDGE,"E29.left"),subQ5,sQuery(id+"F1.wireOp",EDGE,"E30.top"),sQuery(id+"F1.wireOp",EDGE,"E30.left"),subQ4])],"isStart":false}),subQ0,subQ3])],"derivedFrom":subQ3}),makeQuery(id+"F6.boolean.opBoolean","COPY",FACE,{"disambiguationData":[TD([subQ2,subQ0,makeQuery(id+"F3.boolean.opBoolean","COPY",FACE,{"derivedFrom":makeQuery(id+"F3.opExtrude","SWEPT_FACE",FACE,{"disambiguationData":[OSD([sQuery(id+"F0.wireOp",EDGE,"E21")])]})}),subQ3])],"derivedFrom":subQ3})])],"derivedFrom":makeQuery(id+"F8.opExtrude","SWEPT_FACE",FACE,{"disambiguationData":[OSD([sQuery(id+"F7.wireOp",EDGE,"E73")])]})});}
            var Q3;
            {var subQ0=makeQuery(id+"F6.opExtrude","SWEPT_FACE",FACE,{"disambiguationData":[OSD([sQuery(id+"F5.wireOp",EDGE,"E63")])]});Q3=makeQuery(id+"F6.boolean.opBoolean","COPY",FACE,{"disambiguationData":[TD([makeQuery(id+"F2.opExtrude","SWEPT_FACE",FACE,{"disambiguationData":[OSD([sQuery(id+"F1.wireOp",EDGE,"E29.top")])]}),makeQuery(id+"F3.boolean.opBoolean","COPY",FACE,{"derivedFrom":makeQuery(id+"F3.opExtrude","SWEPT_FACE",FACE,{"disambiguationData":[OSD([sQuery(id+"F0.wireOp",EDGE,"E20")])]})}),makeQuery(id+"F3.boolean.opBoolean","COPY",FACE,{"derivedFrom":makeQuery(id+"F3.opExtrude","SWEPT_FACE",FACE,{"disambiguationData":[OSD([sQuery(id+"F0.wireOp",EDGE,"E21")])]})}),subQ0])],"derivedFrom":subQ0});}
            var Q4;
            {var subQ0=sQuery(id+"F1.wireOp",EDGE,"E29.top");var subQ1=makeQuery(id+"F6.opExtrude","SWEPT_FACE",FACE,{"disambiguationData":[OSD([sQuery(id+"F5.wireOp",EDGE,"E62")])]});Q4=makeQuery(id+"F6.boolean.opBoolean","COPY",FACE,{"disambiguationData":[TD([makeQuery(id+"F2.opExtrude","SWEPT_FACE",FACE,{"disambiguationData":[OSD([subQ0])]}),makeQuery(id+"F2.opExtrude","CAP_FACE",FACE,{"disambiguationData":[OSD([subQ0,sQuery(id+"F1.wireOp",EDGE,"E29.left"),sQuery(id+"F1.wireOp",EDGE,"E29.right"),sQuery(id+"F1.wireOp",EDGE,"E30.top"),sQuery(id+"F1.wireOp",EDGE,"E30.left"),sQuery(id+"F1.wireOp",EDGE,"E30.right")])],"isStart":false}),makeQuery(id+"F3.boolean.opBoolean","COPY",FACE,{"derivedFrom":makeQuery(id+"F3.opExtrude","SWEPT_FACE",FACE,{"disambiguationData":[OSD([sQuery(id+"F0.wireOp",EDGE,"E19")])]})}),subQ1])],"derivedFrom":subQ1});}
            var Q5;
            {var subQ0=makeQuery(id+"F6.opExtrude","SWEPT_FACE",FACE,{"disambiguationData":[OSD([sQuery(id+"F5.wireOp",EDGE,"E62")])]});Q5=makeQuery(id+"F6.boolean.opBoolean","COPY",FACE,{"disambiguationData":[TD([makeQuery(id+"F2.opExtrude","SWEPT_FACE",FACE,{"disambiguationData":[OSD([sQuery(id+"F1.wireOp",EDGE,"E29.top")])]}),makeQuery(id+"F3.boolean.opBoolean","COPY",FACE,{"derivedFrom":makeQuery(id+"F3.opExtrude","SWEPT_FACE",FACE,{"disambiguationData":[OSD([sQuery(id+"F0.wireOp",EDGE,"E19")])]})}),makeQuery(id+"F3.boolean.opBoolean","COPY",FACE,{"derivedFrom":makeQuery(id+"F3.opExtrude","SWEPT_FACE",FACE,{"disambiguationData":[OSD([sQuery(id+"F0.wireOp",EDGE,"E22")])]})}),subQ0])],"derivedFrom":subQ0});}
            var Q6;
            {var subQ0=sQuery(id+"F1.wireOp",EDGE,"E29.top");var subQ1=makeQuery(id+"F2.opExtrude","SWEPT_FACE",FACE,{"disambiguationData":[OSD([subQ0])]});var subQ2=makeQuery(id+"F3.boolean.opBoolean","COPY",FACE,{"derivedFrom":makeQuery(id+"F3.opExtrude","SWEPT_FACE",FACE,{"disambiguationData":[OSD([sQuery(id+"F0.wireOp",EDGE,"E18")])]})});var subQ3=makeQuery(id+"F2.opExtrude","CAP_FACE",FACE,{"disambiguationData":[OSD([subQ0,sQuery(id+"F1.wireOp",EDGE,"E29.left"),sQuery(id+"F1.wireOp",EDGE,"E29.right"),sQuery(id+"F1.wireOp",EDGE,"E30.top"),sQuery(id+"F1.wireOp",EDGE,"E30.left"),sQuery(id+"F1.wireOp",EDGE,"E30.right")])],"isStart":false});var subQ4=makeQuery(id+"F6.opExtrude","SWEPT_FACE",FACE,{"disambiguationData":[OSD([sQuery(id+"F5.wireOp",EDGE,"E61")])]});var subQ5=makeQuery(id+"F3.boolean.opBoolean","COPY",FACE,{"derivedFrom":makeQuery(id+"F3.opExtrude","SWEPT_FACE",FACE,{"disambiguationData":[OSD([sQuery(id+"F0.wireOp",EDGE,"E19")])]})});var subQ6=makeQuery(id+"F6.opExtrude","SWEPT_FACE",FACE,{"disambiguationData":[OSD([sQuery(id+"F5.wireOp",EDGE,"E62")])]});Q6=makeQuery(id+"F8.boolean.opBoolean","COPY",FACE,{"disambiguationData":[TD([subQ1,subQ2,subQ5,makeQuery(id+"F6.boolean.opBoolean","COPY",FACE,{"disambiguationData":[TD([subQ1,subQ3,subQ2,subQ4])],"derivedFrom":subQ4}),makeQuery(id+"F6.boolean.opBoolean","COPY",FACE,{"disambiguationData":[TD([subQ1,subQ2,makeQuery(id+"F3.boolean.opBoolean","COPY",FACE,{"derivedFrom":makeQuery(id+"F3.opExtrude","SWEPT_FACE",FACE,{"disambiguationData":[OSD([sQuery(id+"F0.wireOp",EDGE,"E23")])]})}),subQ4])],"derivedFrom":subQ4}),makeQuery(id+"F6.boolean.opBoolean","COPY",FACE,{"disambiguationData":[TD([subQ1,subQ3,subQ5,subQ6])],"derivedFrom":subQ6}),makeQuery(id+"F6.boolean.opBoolean","COPY",FACE,{"disambiguationData":[TD([subQ1,subQ5,makeQuery(id+"F3.boolean.opBoolean","COPY",FACE,{"derivedFrom":makeQuery(id+"F3.opExtrude","SWEPT_FACE",FACE,{"disambiguationData":[OSD([sQuery(id+"F0.wireOp",EDGE,"E22")])]})}),subQ6])],"derivedFrom":subQ6})])],"derivedFrom":makeQuery(id+"F8.opExtrude","SWEPT_FACE",FACE,{"disambiguationData":[OSD([sQuery(id+"F7.wireOp",EDGE,"E73")])]})});}
            var Q7;
            {var subQ0=sQuery(id+"F1.wireOp",EDGE,"E29.top");var subQ1=makeQuery(id+"F6.opExtrude","SWEPT_FACE",FACE,{"disambiguationData":[OSD([sQuery(id+"F5.wireOp",EDGE,"E61")])]});Q7=makeQuery(id+"F6.boolean.opBoolean","COPY",FACE,{"disambiguationData":[TD([makeQuery(id+"F2.opExtrude","SWEPT_FACE",FACE,{"disambiguationData":[OSD([subQ0])]}),makeQuery(id+"F2.opExtrude","CAP_FACE",FACE,{"disambiguationData":[OSD([subQ0,sQuery(id+"F1.wireOp",EDGE,"E29.left"),sQuery(id+"F1.wireOp",EDGE,"E29.right"),sQuery(id+"F1.wireOp",EDGE,"E30.top"),sQuery(id+"F1.wireOp",EDGE,"E30.left"),sQuery(id+"F1.wireOp",EDGE,"E30.right")])],"isStart":false}),makeQuery(id+"F3.boolean.opBoolean","COPY",FACE,{"derivedFrom":makeQuery(id+"F3.opExtrude","SWEPT_FACE",FACE,{"disambiguationData":[OSD([sQuery(id+"F0.wireOp",EDGE,"E18")])]})}),subQ1])],"derivedFrom":subQ1});}
            var Q8;
            {var subQ0=sQuery(id+"F1.wireOp",EDGE,"E29.top");var subQ1=makeQuery(id+"F2.opExtrude","SWEPT_FACE",FACE,{"disambiguationData":[OSD([subQ0])]});var subQ2=makeQuery(id+"F3.boolean.opBoolean","COPY",FACE,{"derivedFrom":makeQuery(id+"F3.opExtrude","SWEPT_FACE",FACE,{"disambiguationData":[OSD([sQuery(id+"F0.wireOp",EDGE,"E18")])]})});var subQ3=sQuery(id+"F1.wireOp",EDGE,"E30.left");var subQ4=sQuery(id+"F1.wireOp",EDGE,"E29.left");var subQ5=makeQuery(id+"F6.opExtrude","SWEPT_FACE",FACE,{"disambiguationData":[OSD([sQuery(id+"F5.wireOp",EDGE,"E61")])]});Q8=makeQuery(id+"F8.boolean.opBoolean","COPY",FACE,{"disambiguationData":[TD([subQ1,makeQuery(id+"F2.opExtrude","SWEPT_FACE",FACE,{"disambiguationData":[OSD([subQ4,subQ3])]}),subQ2,makeQuery(id+"F6.boolean.opBoolean","COPY",FACE,{"disambiguationData":[TD([subQ1,makeQuery(id+"F2.opExtrude","CAP_FACE",FACE,{"disambiguationData":[OSD([subQ0,subQ4,sQuery(id+"F1.wireOp",EDGE,"E29.right"),sQuery(id+"F1.wireOp",EDGE,"E30.top"),subQ3,sQuery(id+"F1.wireOp",EDGE,"E30.right")])],"isStart":false}),subQ2,subQ5])],"derivedFrom":subQ5}),makeQuery(id+"F6.boolean.opBoolean","COPY",FACE,{"disambiguationData":[TD([subQ1,subQ2,makeQuery(id+"F3.boolean.opBoolean","COPY",FACE,{"derivedFrom":makeQuery(id+"F3.opExtrude","SWEPT_FACE",FACE,{"disambiguationData":[OSD([sQuery(id+"F0.wireOp",EDGE,"E23")])]})}),subQ5])],"derivedFrom":subQ5})])],"derivedFrom":makeQuery(id+"F8.opExtrude","SWEPT_FACE",FACE,{"disambiguationData":[OSD([sQuery(id+"F7.wireOp",EDGE,"E73")])]})});}
            var Q9;
            {var subQ0=makeQuery(id+"F6.opExtrude","SWEPT_FACE",FACE,{"disambiguationData":[OSD([sQuery(id+"F5.wireOp",EDGE,"E61")])]});Q9=makeQuery(id+"F6.boolean.opBoolean","COPY",FACE,{"disambiguationData":[TD([makeQuery(id+"F2.opExtrude","SWEPT_FACE",FACE,{"disambiguationData":[OSD([sQuery(id+"F1.wireOp",EDGE,"E29.top")])]}),makeQuery(id+"F3.boolean.opBoolean","COPY",FACE,{"derivedFrom":makeQuery(id+"F3.opExtrude","SWEPT_FACE",FACE,{"disambiguationData":[OSD([sQuery(id+"F0.wireOp",EDGE,"E18")])]})}),makeQuery(id+"F3.boolean.opBoolean","COPY",FACE,{"derivedFrom":makeQuery(id+"F3.opExtrude","SWEPT_FACE",FACE,{"disambiguationData":[OSD([sQuery(id+"F0.wireOp",EDGE,"E23")])]})}),subQ0])],"derivedFrom":subQ0});}
            var Q10;
            {var subQ0=makeQuery(id+"F2.opExtrude","SWEPT_FACE",FACE,{"disambiguationData":[OSD([sQuery(id+"F1.wireOp",EDGE,"E29.top")])]});var subQ1=makeQuery(id+"F3.boolean.opBoolean","COPY",FACE,{"derivedFrom":makeQuery(id+"F3.opExtrude","SWEPT_FACE",FACE,{"disambiguationData":[OSD([sQuery(id+"F0.wireOp",EDGE,"E23")])]})});var subQ2=makeQuery(id+"F6.opExtrude","SWEPT_FACE",FACE,{"disambiguationData":[OSD([sQuery(id+"F5.wireOp",EDGE,"E61")])]});Q10=makeQuery(id+"F8.boolean.opBoolean","COPY",FACE,{"disambiguationData":[TD([subQ0,makeQuery(id+"F2.opExtrude","SWEPT_FACE",FACE,{"disambiguationData":[OSD([sQuery(id+"F1.wireOp",EDGE,"E29.left"),sQuery(id+"F1.wireOp",EDGE,"E30.left")])]}),subQ1,makeQuery(id+"F6.boolean.opBoolean","COPY",FACE,{"disambiguationData":[TD([subQ0,makeQuery(id+"F3.boolean.opBoolean","COPY",FACE,{"derivedFrom":makeQuery(id+"F3.opExtrude","SWEPT_FACE",FACE,{"disambiguationData":[OSD([sQuery(id+"F0.wireOp",EDGE,"E18")])]})}),subQ1,subQ2])],"derivedFrom":subQ2}),makeQuery(id+"F6.boolean.opBoolean","COPY",FACE,{"disambiguationData":[TD([subQ0,subQ1,makeQuery(id+"F3.boolean.opBoolean","COPY",FACE,{"derivedFrom":makeQuery(id+"F3.opExtrude","SWEPT_FACE",FACE,{"disambiguationData":[OSD([sQuery(id+"F0.wireOp",EDGE,"E24")])]})}),subQ2])],"derivedFrom":subQ2})])],"derivedFrom":makeQuery(id+"F8.opExtrude","SWEPT_FACE",FACE,{"disambiguationData":[OSD([sQuery(id+"F7.wireOp",EDGE,"E74")])]})});}
            var Q11;
            {var subQ0=makeQuery(id+"F2.opExtrude","SWEPT_FACE",FACE,{"disambiguationData":[OSD([sQuery(id+"F1.wireOp",EDGE,"E29.top")])]});var subQ1=makeQuery(id+"F3.boolean.opBoolean","COPY",FACE,{"derivedFrom":makeQuery(id+"F3.opExtrude","SWEPT_FACE",FACE,{"disambiguationData":[OSD([sQuery(id+"F0.wireOp",EDGE,"E23")])]})});var subQ2=makeQuery(id+"F6.opExtrude","SWEPT_FACE",FACE,{"disambiguationData":[OSD([sQuery(id+"F5.wireOp",EDGE,"E61")])]});var subQ3=makeQuery(id+"F3.boolean.opBoolean","COPY",FACE,{"derivedFrom":makeQuery(id+"F3.opExtrude","SWEPT_FACE",FACE,{"disambiguationData":[OSD([sQuery(id+"F0.wireOp",EDGE,"E22")])]})});var subQ4=makeQuery(id+"F6.opExtrude","SWEPT_FACE",FACE,{"disambiguationData":[OSD([sQuery(id+"F5.wireOp",EDGE,"E62")])]});Q11=makeQuery(id+"F8.boolean.opBoolean","COPY",FACE,{"disambiguationData":[TD([subQ0,subQ3,subQ1,makeQuery(id+"F6.boolean.opBoolean","COPY",FACE,{"disambiguationData":[TD([subQ0,makeQuery(id+"F3.boolean.opBoolean","COPY",FACE,{"derivedFrom":makeQuery(id+"F3.opExtrude","SWEPT_FACE",FACE,{"disambiguationData":[OSD([sQuery(id+"F0.wireOp",EDGE,"E18")])]})}),subQ1,subQ2])],"derivedFrom":subQ2}),makeQuery(id+"F6.boolean.opBoolean","COPY",FACE,{"disambiguationData":[TD([subQ0,subQ1,makeQuery(id+"F3.boolean.opBoolean","COPY",FACE,{"derivedFrom":makeQuery(id+"F3.opExtrude","SWEPT_FACE",FACE,{"disambiguationData":[OSD([sQuery(id+"F0.wireOp",EDGE,"E24")])]})}),subQ2])],"derivedFrom":subQ2}),makeQuery(id+"F6.boolean.opBoolean","COPY",FACE,{"disambiguationData":[TD([subQ0,makeQuery(id+"F3.boolean.opBoolean","COPY",FACE,{"derivedFrom":makeQuery(id+"F3.opExtrude","SWEPT_FACE",FACE,{"disambiguationData":[OSD([sQuery(id+"F0.wireOp",EDGE,"E19")])]})}),subQ3,subQ4])],"derivedFrom":subQ4}),makeQuery(id+"F6.boolean.opBoolean","COPY",FACE,{"disambiguationData":[TD([subQ0,subQ3,makeQuery(id+"F3.boolean.opBoolean","COPY",FACE,{"derivedFrom":makeQuery(id+"F3.opExtrude","SWEPT_FACE",FACE,{"disambiguationData":[OSD([sQuery(id+"F0.wireOp",EDGE,"E25")])]})}),subQ4])],"derivedFrom":subQ4})])],"derivedFrom":makeQuery(id+"F8.opExtrude","SWEPT_FACE",FACE,{"disambiguationData":[OSD([sQuery(id+"F7.wireOp",EDGE,"E74")])]})});}
            var Q12;
            {var subQ0=makeQuery(id+"F6.opExtrude","SWEPT_FACE",FACE,{"disambiguationData":[OSD([sQuery(id+"F5.wireOp",EDGE,"E61")])]});Q12=makeQuery(id+"F6.boolean.opBoolean","COPY",FACE,{"disambiguationData":[TD([makeQuery(id+"F2.opExtrude","SWEPT_FACE",FACE,{"disambiguationData":[OSD([sQuery(id+"F1.wireOp",EDGE,"E29.top")])]}),makeQuery(id+"F3.boolean.opBoolean","COPY",FACE,{"derivedFrom":makeQuery(id+"F3.opExtrude","SWEPT_FACE",FACE,{"disambiguationData":[OSD([sQuery(id+"F0.wireOp",EDGE,"E23")])]})}),makeQuery(id+"F3.boolean.opBoolean","COPY",FACE,{"derivedFrom":makeQuery(id+"F3.opExtrude","SWEPT_FACE",FACE,{"disambiguationData":[OSD([sQuery(id+"F0.wireOp",EDGE,"E24")])]})}),subQ0])],"derivedFrom":subQ0});}
            var Q13;
            {var subQ0=makeQuery(id+"F6.opExtrude","SWEPT_FACE",FACE,{"disambiguationData":[OSD([sQuery(id+"F5.wireOp",EDGE,"E62")])]});Q13=makeQuery(id+"F6.boolean.opBoolean","COPY",FACE,{"disambiguationData":[TD([makeQuery(id+"F2.opExtrude","SWEPT_FACE",FACE,{"disambiguationData":[OSD([sQuery(id+"F1.wireOp",EDGE,"E29.top")])]}),makeQuery(id+"F3.boolean.opBoolean","COPY",FACE,{"derivedFrom":makeQuery(id+"F3.opExtrude","SWEPT_FACE",FACE,{"disambiguationData":[OSD([sQuery(id+"F0.wireOp",EDGE,"E22")])]})}),makeQuery(id+"F3.boolean.opBoolean","COPY",FACE,{"derivedFrom":makeQuery(id+"F3.opExtrude","SWEPT_FACE",FACE,{"disambiguationData":[OSD([sQuery(id+"F0.wireOp",EDGE,"E25")])]})}),subQ0])],"derivedFrom":subQ0});}
            var Q14;
            {var subQ0=makeQuery(id+"F2.opExtrude","SWEPT_FACE",FACE,{"disambiguationData":[OSD([sQuery(id+"F1.wireOp",EDGE,"E29.top")])]});var subQ1=makeQuery(id+"F3.boolean.opBoolean","COPY",FACE,{"derivedFrom":makeQuery(id+"F3.opExtrude","SWEPT_FACE",FACE,{"disambiguationData":[OSD([sQuery(id+"F0.wireOp",EDGE,"E22")])]})});var subQ2=makeQuery(id+"F6.opExtrude","SWEPT_FACE",FACE,{"disambiguationData":[OSD([sQuery(id+"F5.wireOp",EDGE,"E62")])]});var subQ3=makeQuery(id+"F3.boolean.opBoolean","COPY",FACE,{"derivedFrom":makeQuery(id+"F3.opExtrude","SWEPT_FACE",FACE,{"disambiguationData":[OSD([sQuery(id+"F0.wireOp",EDGE,"E21")])]})});var subQ4=makeQuery(id+"F6.opExtrude","SWEPT_FACE",FACE,{"disambiguationData":[OSD([sQuery(id+"F5.wireOp",EDGE,"E63")])]});Q14=makeQuery(id+"F8.boolean.opBoolean","COPY",FACE,{"disambiguationData":[TD([subQ0,subQ3,subQ1,makeQuery(id+"F6.boolean.opBoolean","COPY",FACE,{"disambiguationData":[TD([subQ0,makeQuery(id+"F3.boolean.opBoolean","COPY",FACE,{"derivedFrom":makeQuery(id+"F3.opExtrude","SWEPT_FACE",FACE,{"disambiguationData":[OSD([sQuery(id+"F0.wireOp",EDGE,"E19")])]})}),subQ1,subQ2])],"derivedFrom":subQ2}),makeQuery(id+"F6.boolean.opBoolean","COPY",FACE,{"disambiguationData":[TD([subQ0,subQ1,makeQuery(id+"F3.boolean.opBoolean","COPY",FACE,{"derivedFrom":makeQuery(id+"F3.opExtrude","SWEPT_FACE",FACE,{"disambiguationData":[OSD([sQuery(id+"F0.wireOp",EDGE,"E25")])]})}),subQ2])],"derivedFrom":subQ2}),makeQuery(id+"F6.boolean.opBoolean","COPY",FACE,{"disambiguationData":[TD([subQ0,makeQuery(id+"F3.boolean.opBoolean","COPY",FACE,{"derivedFrom":makeQuery(id+"F3.opExtrude","SWEPT_FACE",FACE,{"disambiguationData":[OSD([sQuery(id+"F0.wireOp",EDGE,"E20")])]})}),subQ3,subQ4])],"derivedFrom":subQ4}),makeQuery(id+"F6.boolean.opBoolean","COPY",FACE,{"disambiguationData":[TD([subQ0,subQ3,makeQuery(id+"F3.boolean.opBoolean","COPY",FACE,{"derivedFrom":makeQuery(id+"F3.opExtrude","SWEPT_FACE",FACE,{"disambiguationData":[OSD([sQuery(id+"F0.wireOp",EDGE,"E26")])]})}),subQ4])],"derivedFrom":subQ4})])],"derivedFrom":makeQuery(id+"F8.opExtrude","SWEPT_FACE",FACE,{"disambiguationData":[OSD([sQuery(id+"F7.wireOp",EDGE,"E74")])]})});}
            var Q15;
            {var subQ0=makeQuery(id+"F2.opExtrude","SWEPT_FACE",FACE,{"disambiguationData":[OSD([sQuery(id+"F1.wireOp",EDGE,"E29.top")])]});var subQ1=makeQuery(id+"F6.opExtrude","SWEPT_FACE",FACE,{"disambiguationData":[OSD([sQuery(id+"F5.wireOp",EDGE,"E63")])]});var subQ2=makeQuery(id+"F3.boolean.opBoolean","COPY",FACE,{"derivedFrom":makeQuery(id+"F3.opExtrude","SWEPT_FACE",FACE,{"disambiguationData":[OSD([sQuery(id+"F0.wireOp",EDGE,"E21")])]})});Q15=makeQuery(id+"F8.boolean.opBoolean","COPY",FACE,{"disambiguationData":[TD([subQ0,makeQuery(id+"F2.opExtrude","SWEPT_FACE",FACE,{"disambiguationData":[OSD([sQuery(id+"F1.wireOp",EDGE,"E29.right"),sQuery(id+"F1.wireOp",EDGE,"E30.right")])]}),subQ2,makeQuery(id+"F6.boolean.opBoolean","COPY",FACE,{"disambiguationData":[TD([subQ0,makeQuery(id+"F3.boolean.opBoolean","COPY",FACE,{"derivedFrom":makeQuery(id+"F3.opExtrude","SWEPT_FACE",FACE,{"disambiguationData":[OSD([sQuery(id+"F0.wireOp",EDGE,"E20")])]})}),subQ2,subQ1])],"derivedFrom":subQ1}),makeQuery(id+"F6.boolean.opBoolean","COPY",FACE,{"disambiguationData":[TD([subQ0,subQ2,makeQuery(id+"F3.boolean.opBoolean","COPY",FACE,{"derivedFrom":makeQuery(id+"F3.opExtrude","SWEPT_FACE",FACE,{"disambiguationData":[OSD([sQuery(id+"F0.wireOp",EDGE,"E26")])]})}),subQ1])],"derivedFrom":subQ1})])],"derivedFrom":makeQuery(id+"F8.opExtrude","SWEPT_FACE",FACE,{"disambiguationData":[OSD([sQuery(id+"F7.wireOp",EDGE,"E74")])]})});}
            var Q16;
            {var subQ0=makeQuery(id+"F6.opExtrude","SWEPT_FACE",FACE,{"disambiguationData":[OSD([sQuery(id+"F5.wireOp",EDGE,"E63")])]});Q16=makeQuery(id+"F6.boolean.opBoolean","COPY",FACE,{"disambiguationData":[TD([makeQuery(id+"F2.opExtrude","SWEPT_FACE",FACE,{"disambiguationData":[OSD([sQuery(id+"F1.wireOp",EDGE,"E29.top")])]}),makeQuery(id+"F3.boolean.opBoolean","COPY",FACE,{"derivedFrom":makeQuery(id+"F3.opExtrude","SWEPT_FACE",FACE,{"disambiguationData":[OSD([sQuery(id+"F0.wireOp",EDGE,"E21")])]})}),makeQuery(id+"F3.boolean.opBoolean","COPY",FACE,{"derivedFrom":makeQuery(id+"F3.opExtrude","SWEPT_FACE",FACE,{"disambiguationData":[OSD([sQuery(id+"F0.wireOp",EDGE,"E26")])]})}),subQ0])],"derivedFrom":subQ0});}
            var Q17;
            {var subQ0=sQuery(id+"F1.wireOp",EDGE,"E29.top");var subQ1=makeQuery(id+"F2.opExtrude","SWEPT_FACE",FACE,{"disambiguationData":[OSD([subQ0])]});var subQ2=sQuery(id+"F1.wireOp",EDGE,"E30.right");var subQ3=sQuery(id+"F1.wireOp",EDGE,"E29.right");var subQ4=makeQuery(id+"F3.boolean.opBoolean","COPY",FACE,{"derivedFrom":makeQuery(id+"F3.opExtrude","SWEPT_FACE",FACE,{"disambiguationData":[OSD([sQuery(id+"F0.wireOp",EDGE,"E26")])]})});var subQ5=makeQuery(id+"F6.opExtrude","SWEPT_FACE",FACE,{"disambiguationData":[OSD([sQuery(id+"F5.wireOp",EDGE,"E63")])]});Q17=makeQuery(id+"F8.boolean.opBoolean","COPY",FACE,{"disambiguationData":[TD([subQ1,makeQuery(id+"F2.opExtrude","SWEPT_FACE",FACE,{"disambiguationData":[OSD([subQ3,subQ2])]}),subQ4,makeQuery(id+"F6.boolean.opBoolean","COPY",FACE,{"disambiguationData":[TD([subQ1,makeQuery(id+"F2.opExtrude","CAP_FACE",FACE,{"disambiguationData":[OSD([subQ0,sQuery(id+"F1.wireOp",EDGE,"E29.left"),subQ3,sQuery(id+"F1.wireOp",EDGE,"E30.top"),sQuery(id+"F1.wireOp",EDGE,"E30.left"),subQ2])],"isStart":true}),subQ4,subQ5])],"derivedFrom":subQ5}),makeQuery(id+"F6.boolean.opBoolean","COPY",FACE,{"disambiguationData":[TD([subQ1,makeQuery(id+"F3.boolean.opBoolean","COPY",FACE,{"derivedFrom":makeQuery(id+"F3.opExtrude","SWEPT_FACE",FACE,{"disambiguationData":[OSD([sQuery(id+"F0.wireOp",EDGE,"E21")])]})}),subQ4,subQ5])],"derivedFrom":subQ5})])],"derivedFrom":makeQuery(id+"F8.opExtrude","SWEPT_FACE",FACE,{"disambiguationData":[OSD([sQuery(id+"F7.wireOp",EDGE,"E75")])]})});}
            var Q18;
            {var subQ0=sQuery(id+"F1.wireOp",EDGE,"E29.top");var subQ1=makeQuery(id+"F2.opExtrude","SWEPT_FACE",FACE,{"disambiguationData":[OSD([subQ0])]});var subQ2=makeQuery(id+"F2.opExtrude","CAP_FACE",FACE,{"disambiguationData":[OSD([subQ0,sQuery(id+"F1.wireOp",EDGE,"E29.left"),sQuery(id+"F1.wireOp",EDGE,"E29.right"),sQuery(id+"F1.wireOp",EDGE,"E30.top"),sQuery(id+"F1.wireOp",EDGE,"E30.left"),sQuery(id+"F1.wireOp",EDGE,"E30.right")])],"isStart":true});var subQ3=makeQuery(id+"F6.opExtrude","SWEPT_FACE",FACE,{"disambiguationData":[OSD([sQuery(id+"F5.wireOp",EDGE,"E62")])]});var subQ4=makeQuery(id+"F3.boolean.opBoolean","COPY",FACE,{"derivedFrom":makeQuery(id+"F3.opExtrude","SWEPT_FACE",FACE,{"disambiguationData":[OSD([sQuery(id+"F0.wireOp",EDGE,"E25")])]})});var subQ5=makeQuery(id+"F3.boolean.opBoolean","COPY",FACE,{"derivedFrom":makeQuery(id+"F3.opExtrude","SWEPT_FACE",FACE,{"disambiguationData":[OSD([sQuery(id+"F0.wireOp",EDGE,"E26")])]})});var subQ6=makeQuery(id+"F6.opExtrude","SWEPT_FACE",FACE,{"disambiguationData":[OSD([sQuery(id+"F5.wireOp",EDGE,"E63")])]});Q18=makeQuery(id+"F8.boolean.opBoolean","COPY",FACE,{"disambiguationData":[TD([subQ1,subQ4,subQ5,makeQuery(id+"F6.boolean.opBoolean","COPY",FACE,{"disambiguationData":[TD([subQ1,subQ2,subQ4,subQ3])],"derivedFrom":subQ3}),makeQuery(id+"F6.boolean.opBoolean","COPY",FACE,{"disambiguationData":[TD([subQ1,makeQuery(id+"F3.boolean.opBoolean","COPY",FACE,{"derivedFrom":makeQuery(id+"F3.opExtrude","SWEPT_FACE",FACE,{"disambiguationData":[OSD([sQuery(id+"F0.wireOp",EDGE,"E22")])]})}),subQ4,subQ3])],"derivedFrom":subQ3}),makeQuery(id+"F6.boolean.opBoolean","COPY",FACE,{"disambiguationData":[TD([subQ1,subQ2,subQ5,subQ6])],"derivedFrom":subQ6}),makeQuery(id+"F6.boolean.opBoolean","COPY",FACE,{"disambiguationData":[TD([subQ1,makeQuery(id+"F3.boolean.opBoolean","COPY",FACE,{"derivedFrom":makeQuery(id+"F3.opExtrude","SWEPT_FACE",FACE,{"disambiguationData":[OSD([sQuery(id+"F0.wireOp",EDGE,"E21")])]})}),subQ5,subQ6])],"derivedFrom":subQ6})])],"derivedFrom":makeQuery(id+"F8.opExtrude","SWEPT_FACE",FACE,{"disambiguationData":[OSD([sQuery(id+"F7.wireOp",EDGE,"E75")])]})});}
            var Q19;
            {var subQ0=sQuery(id+"F1.wireOp",EDGE,"E29.top");var subQ1=makeQuery(id+"F2.opExtrude","SWEPT_FACE",FACE,{"disambiguationData":[OSD([subQ0])]});var subQ2=makeQuery(id+"F2.opExtrude","CAP_FACE",FACE,{"disambiguationData":[OSD([subQ0,sQuery(id+"F1.wireOp",EDGE,"E29.left"),sQuery(id+"F1.wireOp",EDGE,"E29.right"),sQuery(id+"F1.wireOp",EDGE,"E30.top"),sQuery(id+"F1.wireOp",EDGE,"E30.left"),sQuery(id+"F1.wireOp",EDGE,"E30.right")])],"isStart":true});var subQ3=makeQuery(id+"F3.boolean.opBoolean","COPY",FACE,{"derivedFrom":makeQuery(id+"F3.opExtrude","SWEPT_FACE",FACE,{"disambiguationData":[OSD([sQuery(id+"F0.wireOp",EDGE,"E24")])]})});var subQ4=makeQuery(id+"F6.opExtrude","SWEPT_FACE",FACE,{"disambiguationData":[OSD([sQuery(id+"F5.wireOp",EDGE,"E61")])]});var subQ5=makeQuery(id+"F3.boolean.opBoolean","COPY",FACE,{"derivedFrom":makeQuery(id+"F3.opExtrude","SWEPT_FACE",FACE,{"disambiguationData":[OSD([sQuery(id+"F0.wireOp",EDGE,"E25")])]})});var subQ6=makeQuery(id+"F6.opExtrude","SWEPT_FACE",FACE,{"disambiguationData":[OSD([sQuery(id+"F5.wireOp",EDGE,"E62")])]});Q19=makeQuery(id+"F8.boolean.opBoolean","COPY",FACE,{"disambiguationData":[TD([subQ1,subQ3,subQ5,makeQuery(id+"F6.boolean.opBoolean","COPY",FACE,{"disambiguationData":[TD([subQ1,subQ2,subQ3,subQ4])],"derivedFrom":subQ4}),makeQuery(id+"F6.boolean.opBoolean","COPY",FACE,{"disambiguationData":[TD([subQ1,makeQuery(id+"F3.boolean.opBoolean","COPY",FACE,{"derivedFrom":makeQuery(id+"F3.opExtrude","SWEPT_FACE",FACE,{"disambiguationData":[OSD([sQuery(id+"F0.wireOp",EDGE,"E23")])]})}),subQ3,subQ4])],"derivedFrom":subQ4}),makeQuery(id+"F6.boolean.opBoolean","COPY",FACE,{"disambiguationData":[TD([subQ1,subQ2,subQ5,subQ6])],"derivedFrom":subQ6}),makeQuery(id+"F6.boolean.opBoolean","COPY",FACE,{"disambiguationData":[TD([subQ1,makeQuery(id+"F3.boolean.opBoolean","COPY",FACE,{"derivedFrom":makeQuery(id+"F3.opExtrude","SWEPT_FACE",FACE,{"disambiguationData":[OSD([sQuery(id+"F0.wireOp",EDGE,"E22")])]})}),subQ5,subQ6])],"derivedFrom":subQ6})])],"derivedFrom":makeQuery(id+"F8.opExtrude","SWEPT_FACE",FACE,{"disambiguationData":[OSD([sQuery(id+"F7.wireOp",EDGE,"E75")])]})});}
            var Q20;
            {var subQ0=makeQuery(id+"F3.boolean.opBoolean","COPY",FACE,{"derivedFrom":makeQuery(id+"F3.opExtrude","SWEPT_FACE",FACE,{"disambiguationData":[OSD([sQuery(id+"F0.wireOp",EDGE,"E24")])]})});var subQ1=sQuery(id+"F1.wireOp",EDGE,"E29.top");var subQ2=makeQuery(id+"F2.opExtrude","SWEPT_FACE",FACE,{"disambiguationData":[OSD([subQ1])]});var subQ3=sQuery(id+"F1.wireOp",EDGE,"E30.left");var subQ4=sQuery(id+"F1.wireOp",EDGE,"E29.left");var subQ5=makeQuery(id+"F6.opExtrude","SWEPT_FACE",FACE,{"disambiguationData":[OSD([sQuery(id+"F5.wireOp",EDGE,"E61")])]});Q20=makeQuery(id+"F8.boolean.opBoolean","COPY",FACE,{"disambiguationData":[TD([subQ2,makeQuery(id+"F2.opExtrude","SWEPT_FACE",FACE,{"disambiguationData":[OSD([subQ4,subQ3])]}),subQ0,makeQuery(id+"F6.boolean.opBoolean","COPY",FACE,{"disambiguationData":[TD([subQ2,makeQuery(id+"F2.opExtrude","CAP_FACE",FACE,{"disambiguationData":[OSD([subQ1,subQ4,sQuery(id+"F1.wireOp",EDGE,"E29.right"),sQuery(id+"F1.wireOp",EDGE,"E30.top"),subQ3,sQuery(id+"F1.wireOp",EDGE,"E30.right")])],"isStart":true}),subQ0,subQ5])],"derivedFrom":subQ5}),makeQuery(id+"F6.boolean.opBoolean","COPY",FACE,{"disambiguationData":[TD([subQ2,makeQuery(id+"F3.boolean.opBoolean","COPY",FACE,{"derivedFrom":makeQuery(id+"F3.opExtrude","SWEPT_FACE",FACE,{"disambiguationData":[OSD([sQuery(id+"F0.wireOp",EDGE,"E23")])]})}),subQ0,subQ5])],"derivedFrom":subQ5})])],"derivedFrom":makeQuery(id+"F8.opExtrude","SWEPT_FACE",FACE,{"disambiguationData":[OSD([sQuery(id+"F7.wireOp",EDGE,"E75")])]})});}
            var Q21;
            {var subQ0=sQuery(id+"F1.wireOp",EDGE,"E29.top");var subQ1=makeQuery(id+"F6.opExtrude","SWEPT_FACE",FACE,{"disambiguationData":[OSD([sQuery(id+"F5.wireOp",EDGE,"E61")])]});Q21=makeQuery(id+"F6.boolean.opBoolean","COPY",FACE,{"disambiguationData":[TD([makeQuery(id+"F2.opExtrude","SWEPT_FACE",FACE,{"disambiguationData":[OSD([subQ0])]}),makeQuery(id+"F2.opExtrude","CAP_FACE",FACE,{"disambiguationData":[OSD([subQ0,sQuery(id+"F1.wireOp",EDGE,"E29.left"),sQuery(id+"F1.wireOp",EDGE,"E29.right"),sQuery(id+"F1.wireOp",EDGE,"E30.top"),sQuery(id+"F1.wireOp",EDGE,"E30.left"),sQuery(id+"F1.wireOp",EDGE,"E30.right")])],"isStart":true}),makeQuery(id+"F3.boolean.opBoolean","COPY",FACE,{"derivedFrom":makeQuery(id+"F3.opExtrude","SWEPT_FACE",FACE,{"disambiguationData":[OSD([sQuery(id+"F0.wireOp",EDGE,"E24")])]})}),subQ1])],"derivedFrom":subQ1});}
            var Q22;
            {var subQ0=sQuery(id+"F1.wireOp",EDGE,"E29.top");var subQ1=makeQuery(id+"F6.opExtrude","SWEPT_FACE",FACE,{"disambiguationData":[OSD([sQuery(id+"F5.wireOp",EDGE,"E62")])]});Q22=makeQuery(id+"F6.boolean.opBoolean","COPY",FACE,{"disambiguationData":[TD([makeQuery(id+"F2.opExtrude","SWEPT_FACE",FACE,{"disambiguationData":[OSD([subQ0])]}),makeQuery(id+"F2.opExtrude","CAP_FACE",FACE,{"disambiguationData":[OSD([subQ0,sQuery(id+"F1.wireOp",EDGE,"E29.left"),sQuery(id+"F1.wireOp",EDGE,"E29.right"),sQuery(id+"F1.wireOp",EDGE,"E30.top"),sQuery(id+"F1.wireOp",EDGE,"E30.left"),sQuery(id+"F1.wireOp",EDGE,"E30.right")])],"isStart":true}),makeQuery(id+"F3.boolean.opBoolean","COPY",FACE,{"derivedFrom":makeQuery(id+"F3.opExtrude","SWEPT_FACE",FACE,{"disambiguationData":[OSD([sQuery(id+"F0.wireOp",EDGE,"E25")])]})}),subQ1])],"derivedFrom":subQ1});}
            var Q23;
            {var subQ0=sQuery(id+"F1.wireOp",EDGE,"E29.top");var subQ1=makeQuery(id+"F6.opExtrude","SWEPT_FACE",FACE,{"disambiguationData":[OSD([sQuery(id+"F5.wireOp",EDGE,"E63")])]});Q23=makeQuery(id+"F6.boolean.opBoolean","COPY",FACE,{"disambiguationData":[TD([makeQuery(id+"F2.opExtrude","SWEPT_FACE",FACE,{"disambiguationData":[OSD([subQ0])]}),makeQuery(id+"F2.opExtrude","CAP_FACE",FACE,{"disambiguationData":[OSD([subQ0,sQuery(id+"F1.wireOp",EDGE,"E29.left"),sQuery(id+"F1.wireOp",EDGE,"E29.right"),sQuery(id+"F1.wireOp",EDGE,"E30.top"),sQuery(id+"F1.wireOp",EDGE,"E30.left"),sQuery(id+"F1.wireOp",EDGE,"E30.right")])],"isStart":true}),makeQuery(id+"F3.boolean.opBoolean","COPY",FACE,{"derivedFrom":makeQuery(id+"F3.opExtrude","SWEPT_FACE",FACE,{"disambiguationData":[OSD([sQuery(id+"F0.wireOp",EDGE,"E26")])]})}),subQ1])],"derivedFrom":subQ1});}
            fillet(context, id + "F15", {"entities" : qUnion([Q0, Q1, Q2, Q3, Q4, Q5, Q6, Q7, Q8, Q9, Q10, Q11, Q12, Q13, Q14, Q15, Q16, Q17, Q18, Q19, Q20, Q21, Q22, Q23]), "radius" : .5 * mm, "tangentPropagation" : true, "allowEdgeOverflow" : false});
        }
        {
            var Q0;
            Q0=makeQuery(id+"F3.boolean.opBoolean","COPY",FACE,{"derivedFrom":makeQuery(id+"F3.opExtrude","SWEPT_FACE",FACE,{"disambiguationData":[OSD([sQuery(id+"F0.wireOp",EDGE,"E24")])]})});
            var Q1;
            Q1=makeQuery(id+"F3.boolean.opBoolean","COPY",FACE,{"derivedFrom":makeQuery(id+"F3.opExtrude","SWEPT_FACE",FACE,{"disambiguationData":[OSD([sQuery(id+"F0.wireOp",EDGE,"E23")])]})});
            var Q2;
            Q2=makeQuery(id+"F3.boolean.opBoolean","COPY",FACE,{"derivedFrom":makeQuery(id+"F3.opExtrude","SWEPT_FACE",FACE,{"disambiguationData":[OSD([sQuery(id+"F0.wireOp",EDGE,"E18")])]})});
            var Q3;
            Q3=makeQuery(id+"F3.boolean.opBoolean","COPY",FACE,{"derivedFrom":makeQuery(id+"F3.opExtrude","SWEPT_FACE",FACE,{"disambiguationData":[OSD([sQuery(id+"F0.wireOp",EDGE,"E25")])]})});
            var Q4;
            Q4=makeQuery(id+"F3.boolean.opBoolean","COPY",FACE,{"derivedFrom":makeQuery(id+"F3.opExtrude","SWEPT_FACE",FACE,{"disambiguationData":[OSD([sQuery(id+"F0.wireOp",EDGE,"E22")])]})});
            var Q5;
            Q5=makeQuery(id+"F3.boolean.opBoolean","COPY",FACE,{"derivedFrom":makeQuery(id+"F3.opExtrude","SWEPT_FACE",FACE,{"disambiguationData":[OSD([sQuery(id+"F0.wireOp",EDGE,"E19")])]})});
            var Q6;
            Q6=makeQuery(id+"F3.boolean.opBoolean","COPY",FACE,{"derivedFrom":makeQuery(id+"F3.opExtrude","SWEPT_FACE",FACE,{"disambiguationData":[OSD([sQuery(id+"F0.wireOp",EDGE,"E26")])]})});
            var Q7;
            Q7=makeQuery(id+"F3.boolean.opBoolean","COPY",FACE,{"derivedFrom":makeQuery(id+"F3.opExtrude","SWEPT_FACE",FACE,{"disambiguationData":[OSD([sQuery(id+"F0.wireOp",EDGE,"E21")])]})});
            var Q8;
            Q8=makeQuery(id+"F3.boolean.opBoolean","COPY",FACE,{"derivedFrom":makeQuery(id+"F3.opExtrude","SWEPT_FACE",FACE,{"disambiguationData":[OSD([sQuery(id+"F0.wireOp",EDGE,"E20")])]})});
            fillet(context, id + "F16", {"entities" : qUnion([Q0, Q1, Q2, Q3, Q4, Q5, Q6, Q7, Q8]), "radius" : 1 * mm, "tangentPropagation" : true, "allowEdgeOverflow" : false});
        }
    });
